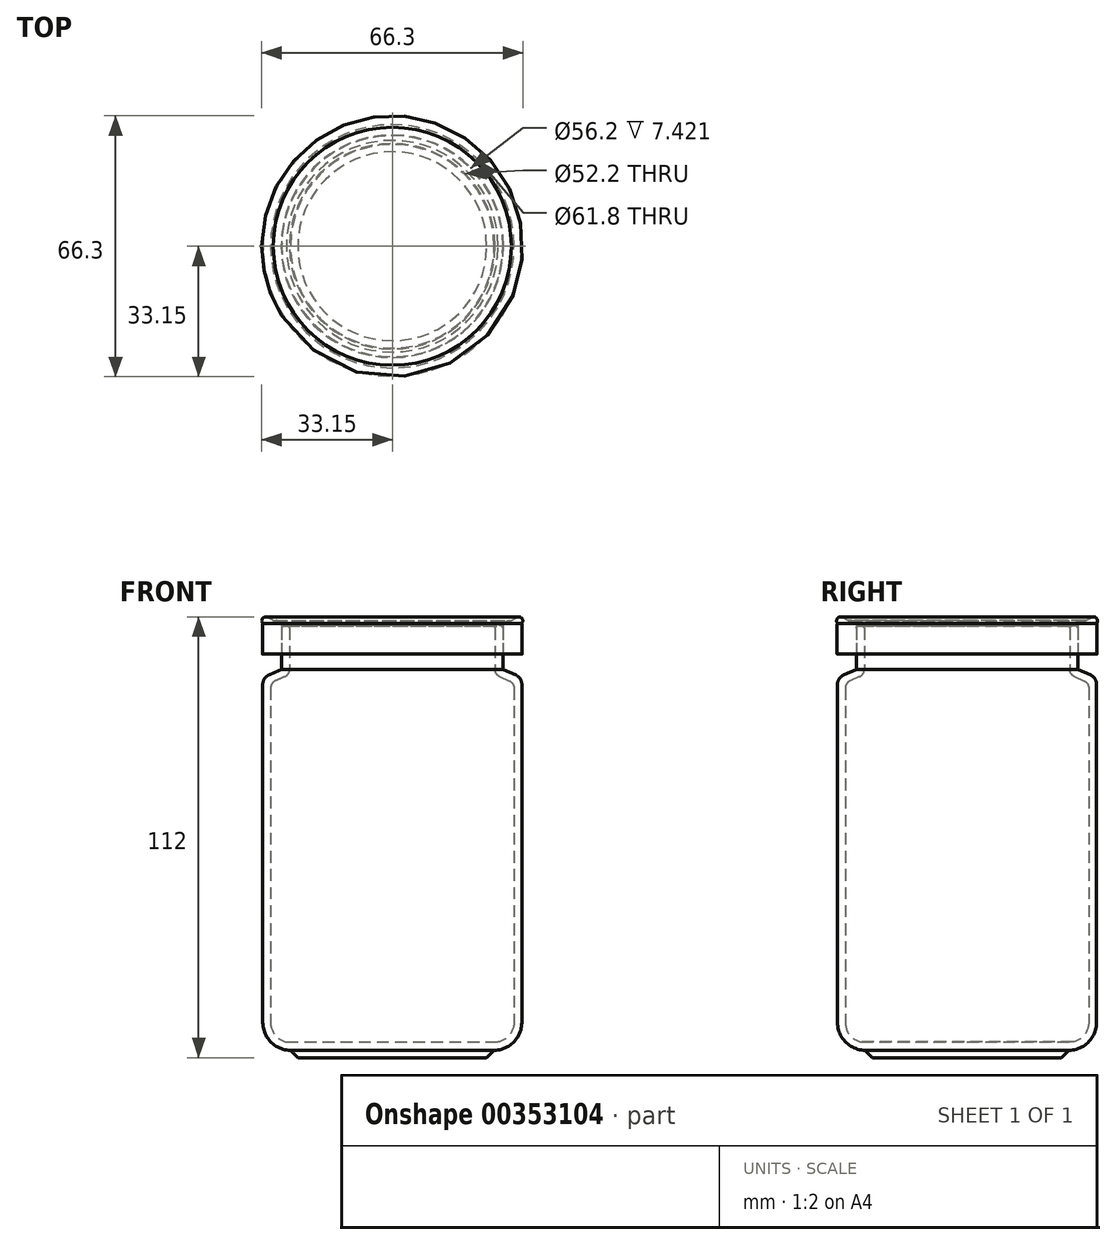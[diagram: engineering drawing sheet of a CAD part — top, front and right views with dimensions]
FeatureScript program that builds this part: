
annotation { "Feature Type Name" : "Feature", "Feature Type Description" : "" }
export const myFeature = defineFeature(function(context is Context, id is Id, definition is map)
    precondition{}
    {
        {
            var Q0;
            Q0=qCreatedBy(makeId("Front.planeOp"),FACE);
            var sketch = newSketch(context, id + "F0", { "sketchPlane" : qUnion([Q0])});
            skLineSegment(sketch, "E0", {"start": v(0, 0) * mm, "end": v(24, 0) * mm});
            skLineSegment(sketch, "E1", {"start": v(24, 0) * mm, "end": v(25.9, 1.9) * mm});
            skArc(sketch, "E2", {"start": v(25.9, 1.9) * mm, "mid": v(30.85, 3.95) * mm, "end": v(32.9, 8.9) * mm});
            skLineSegment(sketch, "E3", {"start": v(32.9, 8.9) * mm, "end": v(32.9, 94.9) * mm});
            skArc(sketch, "E4", {"start": v(32.9, 94.9) * mm, "mid": v(32.5, 96.26) * mm, "end": v(31.41, 97.19) * mm});
            skLineSegment(sketch, "E5", {"start": v(31.41, 97.19) * mm, "end": v(28.1, 98.65) * mm});
            skLineSegment(sketch, "E6", {"start": v(28.1, 98.65) * mm, "end": v(28.1, 109.15) * mm});
            skLineSegment(sketch, "E7.0", {"start": v(26.1, 98.65) * mm, "end": v(26.1, 109.15) * mm});
            skLineSegment(sketch, "E7.1", {"start": v(29.7, 95.75) * mm, "end": v(27.3, 96.82) * mm});
            skLineSegment(sketch, "E7.2", {"start": v(30.9, 8.9) * mm, "end": v(30.9, 93.92) * mm});
            skLineSegment(sketch, "E8", {"start": v(26.6, 109.65) * mm, "end": v(27.6, 109.65) * mm});
            skPoint(sketch, "E9.visualSharp", {"position": v(26.1, 109.65) * mm});
            skArc(sketch, "E9.filletArc", {"start": v(26.6, 109.65) * mm, "mid": v(26.25, 109.5) * mm, "end": v(26.1, 109.15) * mm});
            skPoint(sketch, "E10.visualSharp", {"position": v(28.1, 109.65) * mm});
            skArc(sketch, "E10.filletArc", {"start": v(28.1, 109.15) * mm, "mid": v(27.95, 109.5) * mm, "end": v(27.6, 109.65) * mm});
            skPoint(sketch, "E11.visualSharp", {"position": v(26.1, 97.35) * mm});
            skArc(sketch, "E11.filletArc", {"start": v(26.1, 98.65) * mm, "mid": v(26.42, 97.56) * mm, "end": v(27.3, 96.82) * mm});
            skPoint(sketch, "E12.visualSharp", {"position": v(30.9, 95.23) * mm});
            skArc(sketch, "E12.filletArc", {"start": v(30.9, 93.92) * mm, "mid": v(30.58, 95.01) * mm, "end": v(29.7, 95.75) * mm});
            skArc(sketch, "E13.filletArc", {"start": v(26.9, 4) * mm, "mid": v(29.77, 5.74) * mm, "end": v(30.9, 8.9) * mm});
            skLineSegment(sketch, "E14", {"start": v(26.9, 4) * mm, "end": v(0, 4) * mm});
            skLineSegment(sketch, "E15", {"start": v(0, 0) * mm, "end": v(0, 55.91) * mm, "construction": true});
            skLineSegment(sketch, "E16", {"start": v(0, 4) * mm, "end": v(0, 0) * mm});
            skSolve(sketch);
        }
        {
            var Q0;
            Q0=qCreatedBy(makeId("Front.planeOp"),FACE);
            var sketch = newSketch(context, id + "F1", { "sketchPlane" : qUnion([Q0])});
            skLineSegment(sketch, "E17", {"start": v(28.1, 102.5) * mm, "end": v(32.95, 102.5) * mm});
            skLineSegment(sketch, "E18", {"start": v(33, 102.56) * mm, "end": v(33, 110) * mm});
            skLineSegment(sketch, "E19", {"start": v(32.5, 110.5) * mm, "end": v(32.15, 110.5) * mm});
            skLineSegment(sketch, "E20", {"start": v(31.8, 110.65) * mm, "end": v(31.5, 110.95) * mm});
            skLineSegment(sketch, "E21", {"start": v(31.15, 111.1) * mm, "end": v(29.56, 111.1) * mm});
            skLineSegment(sketch, "E22", {"start": v(29.2, 110.95) * mm, "end": v(28.91, 110.65) * mm});
            skLineSegment(sketch, "E23", {"start": v(28.56, 110.5) * mm, "end": v(0, 110.5) * mm});
            skPoint(sketch, "E24.visualSharp", {"position": v(28.76, 110.5) * mm});
            skArc(sketch, "E24.filletArc", {"start": v(28.56, 110.5) * mm, "mid": v(28.75, 110.54) * mm, "end": v(28.91, 110.65) * mm});
            skPoint(sketch, "E25.visualSharp", {"position": v(29.35, 111.1) * mm});
            skArc(sketch, "E25.filletArc", {"start": v(29.56, 111.1) * mm, "mid": v(29.37, 111.05) * mm, "end": v(29.2, 110.95) * mm});
            skPoint(sketch, "E26.visualSharp", {"position": v(31.35, 111.1) * mm});
            skArc(sketch, "E26.filletArc", {"start": v(31.5, 110.95) * mm, "mid": v(31.34, 111.05) * mm, "end": v(31.15, 111.1) * mm});
            skPoint(sketch, "E27.visualSharp", {"position": v(31.94, 110.5) * mm});
            skArc(sketch, "E27.filletArc", {"start": v(31.8, 110.65) * mm, "mid": v(31.96, 110.54) * mm, "end": v(32.15, 110.5) * mm});
            skPoint(sketch, "E28.visualSharp", {"position": v(33, 110.5) * mm});
            skArc(sketch, "E28.filletArc", {"start": v(33, 110) * mm, "mid": v(32.85, 110.36) * mm, "end": v(32.5, 110.5) * mm});
            skPoint(sketch, "E29.visualSharp", {"position": v(33, 102.5) * mm});
            skArc(sketch, "E29.filletArc", {"start": v(32.95, 102.5) * mm, "mid": v(32.98, 102.52) * mm, "end": v(33, 102.56) * mm});
            skLineSegment(sketch, "E30.0", {"start": v(28.56, 110) * mm, "end": v(0, 110) * mm});
            skArc(sketch, "E30.1", {"start": v(28.56, 110) * mm, "mid": v(28.94, 110.08) * mm, "end": v(29.26, 110.3) * mm});
            skArc(sketch, "E30.2", {"start": v(31.44, 110.3) * mm, "mid": v(33.14, 110.86) * mm, "end": v(31.67, 111.88) * mm});
            skLineSegment(sketch, "E30.3", {"start": v(31.44, 110.3) * mm, "end": v(31.15, 110.6) * mm});
            skLineSegment(sketch, "E30.4", {"start": v(31.15, 110.6) * mm, "end": v(29.56, 110.6) * mm});
            skLineSegment(sketch, "E30.5", {"start": v(29.56, 110.6) * mm, "end": v(29.26, 110.3) * mm});
            skLineSegment(sketch, "E31", {"start": v(0, 110.5) * mm, "end": v(0, 110) * mm});
            skLineSegment(sketch, "E32", {"start": v(28.1, 102.5) * mm, "end": v(28.1, 103.4) * mm});
            skLineSegment(sketch, "E33", {"start": v(28.1, 103.4) * mm, "end": v(28.1, 109.92) * mm});
            skLineSegment(sketch, "E34", {"start": v(28.1, 109.92) * mm, "end": v(31.67, 111.88) * mm});
            skSolve(sketch);
        }
        {
            var Q0;
            Q0=qSketchRegion(id+"F1",true);
            var Q1;
            Q1=sQuery(id+"F0.wireOp",EDGE,"E15");
            revolve(context, id + "F2", {"entities" : qUnion([Q0]), "axis" : qUnion([Q1]), "revolveType" : RevolveType.FULL});
        }
        {
            var Q0;
            Q0=qSketchRegion(id+"F0",true);
            var Q1;
            Q1=sQuery(id+"F0.wireOp",EDGE,"E15");
            revolve(context, id + "F3", {"entities" : qUnion([Q0]), "axis" : qUnion([Q1]), "revolveType" : RevolveType.FULL});
        }
    });
